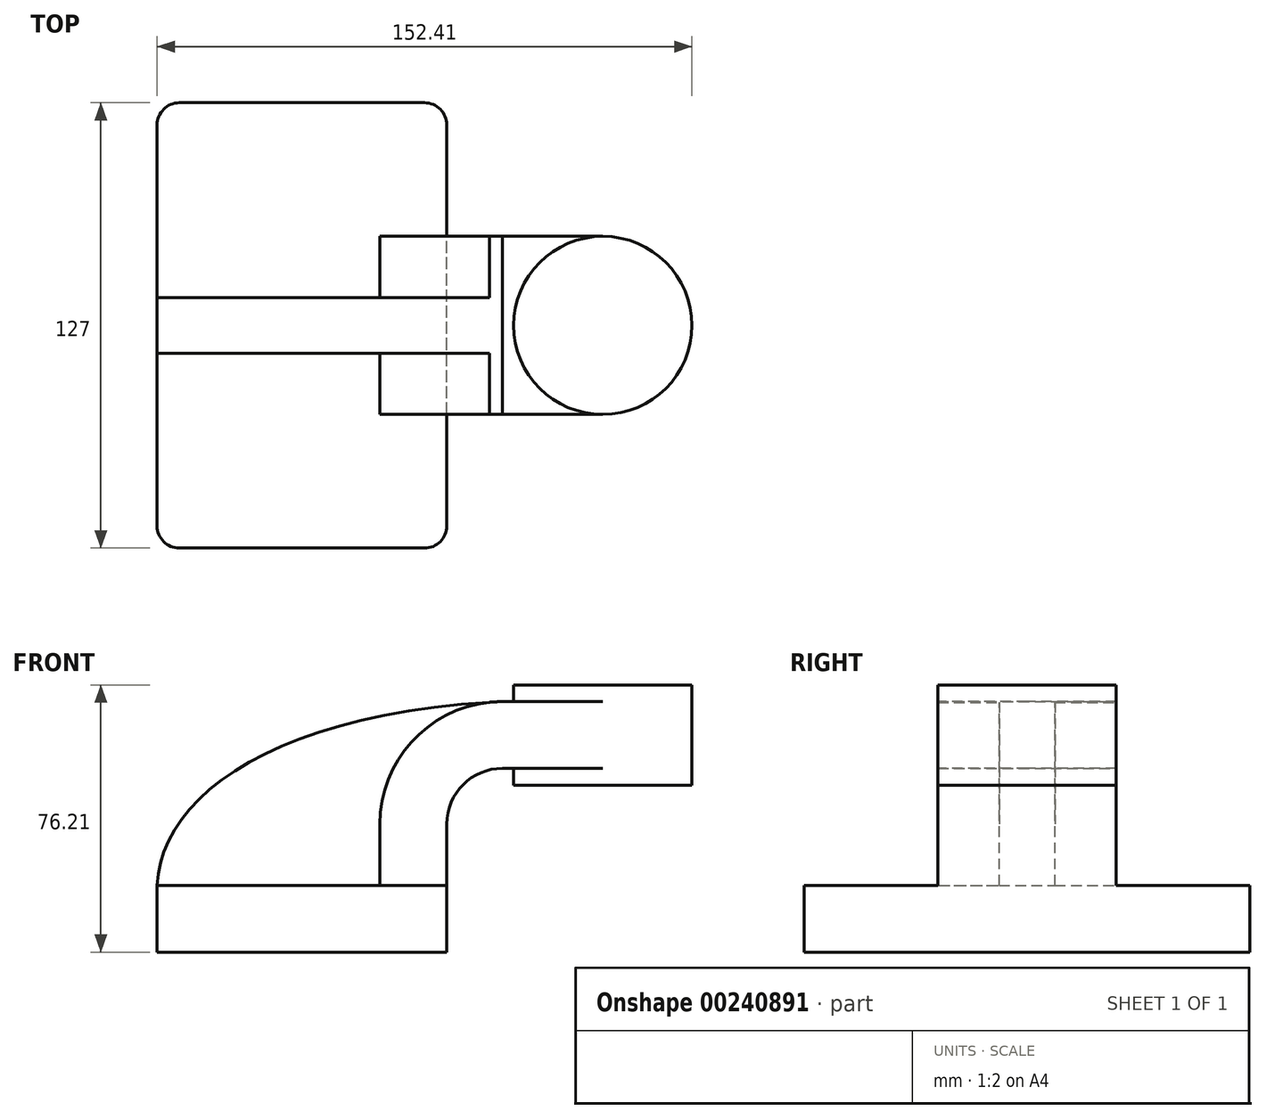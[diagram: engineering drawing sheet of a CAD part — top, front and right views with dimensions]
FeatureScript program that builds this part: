
annotation { "Feature Type Name" : "Feature", "Feature Type Description" : "" }
export const myFeature = defineFeature(function(context is Context, id is Id, definition is map)
    precondition{}
    {
        {
            var Q0;
            Q0=qCreatedBy(makeId("Front.planeOp"),FACE);
            var sketch = newSketch(context, id + "F0", { "sketchPlane" : qUnion([Q0])});
            skLineSegment(sketch, "E0.bottom", {"start": v(41.27, 9.53) * mm, "end": v(-41.28, 9.53) * mm});
            skLineSegment(sketch, "E0.top", {"start": v(41.28, -9.52) * mm, "end": v(-41.27, -9.52) * mm});
            skLineSegment(sketch, "E0.left", {"start": v(41.28, 9.53) * mm, "end": v(41.28, -9.52) * mm});
            skLineSegment(sketch, "E0.right", {"start": v(-41.28, 9.53) * mm, "end": v(-41.27, -9.52) * mm});
            skPoint(sketch, "E0.middle", {"position": v(0, 0) * mm});
            skLineSegment(sketch, "E1.bottom", {"start": v(111.12, 38.1) * mm, "end": v(60.32, 38.1) * mm});
            skLineSegment(sketch, "E1.top", {"start": v(111.12, 66.68) * mm, "end": v(60.32, 66.68) * mm});
            skLineSegment(sketch, "E1.left", {"start": v(111.12, 38.1) * mm, "end": v(111.12, 66.68) * mm});
            skLineSegment(sketch, "E1.right", {"start": v(60.32, 38.1) * mm, "end": v(60.32, 66.68) * mm});
            skPoint(sketch, "E1.middle", {"position": v(85.72, 52.39) * mm});
            skLineSegment(sketch, "E2", {"start": v(41.27, 9.53) * mm, "end": v(41.27, 27) * mm});
            skArc(sketch, "E3", {"start": v(41.27, 27) * mm, "mid": v(45.92, 38.23) * mm, "end": v(57.15, 42.88) * mm});
            skLineSegment(sketch, "E4", {"start": v(57.15, 42.88) * mm, "end": v(98.13, 42.88) * mm});
            skLineSegment(sketch, "E5.0", {"start": v(57.15, 61.93) * mm, "end": v(98.13, 61.93) * mm});
            skArc(sketch, "E5.1", {"start": v(22.23, 27) * mm, "mid": v(32.45, 51.7) * mm, "end": v(57.15, 61.93) * mm});
            skLineSegment(sketch, "E5.2", {"start": v(22.22, 9.53) * mm, "end": v(22.22, 27) * mm});
            skLineSegment(sketch, "E6", {"start": v(85.72, 38.1) * mm, "end": v(85.73, 66.68) * mm});
            skFitSpline(sketch, "E7", {"points": [v(-41.28, 9.52) * mm, v(57.15, 61.93) * mm], "startDerivative": vector(3.13, 75.02) * mm, "endDerivative": vector(196.2, 9.22) * mm});
            skSolve(sketch);
        }
        {
            var Q0;
            Q0=makeQuery(id+"F0.imprint","IMPRINT",FACE,{"disambiguationData":[TD([[makeQuery(id+"F0.imprint","IMPRINT",EDGE,{"derivedFrom":sQuery(id+"F0.wireOp",EDGE,"E0.top")}),-1.0]])]});
            extrude(context, id + "F1", {"entities" : qUnion([Q0]), "endBound" : BoundingType.SYMMETRIC, "depth" : 127 * mm});
        }
        {
            var Q0;
            {var subQ0=sQuery(id+"F0.wireOp",EDGE,"E4");var subQ1=sQuery(id+"F0.wireOp",EDGE,"E1.right");var subQ2=makeQuery(id+"F0.imprint","INTERSECT",VERTEX,{"derivedFrom":[subQ1,subQ0]});Q0=makeQuery(id+"F0.imprint","IMPRINT",FACE,{"disambiguationData":[TD([[makeQuery(id+"F0.imprint","IMPRINT",EDGE,{"disambiguationData":[TD([[subQ2,-1.0]])],"derivedFrom":subQ1}),-1.0]])]});}
            var Q1;
            {var subQ1=sQuery(id+"F0.wireOp",EDGE,"E2");Q1=makeQuery(id+"F0.imprint","IMPRINT",FACE,{"disambiguationData":[TD([[makeQuery(id+"F0.imprint","IMPRINT",EDGE,{"derivedFrom":subQ1}),1.0]])]});}
            extrude(context, id + "F2", {"entities" : qUnion([Q0, Q1]), "operationType" : NewBodyOperationType.ADD, "endBound" : BoundingType.SYMMETRIC, "depth" : 50.8 * mm});
        }
        {
            var Q0;
            {var subQ3=sQuery(id+"F0.wireOp",EDGE,"E5.2");Q0=makeQuery(id+"F0.imprint","IMPRINT",FACE,{"disambiguationData":[TD([[makeQuery(id+"F0.imprint","IMPRINT",EDGE,{"derivedFrom":subQ3}),1.0]])]});}
            extrude(context, id + "F3", {"entities" : qUnion([Q0]), "operationType" : NewBodyOperationType.ADD, "endBound" : BoundingType.SYMMETRIC, "depth" : 15.88 * mm});
        }
        {
            var Q0;
            {var subQ0=sQuery(id+"F0.wireOp",EDGE,"E1.left");Q0=makeQuery(id+"F0.imprint","IMPRINT",FACE,{"disambiguationData":[TD([[makeQuery(id+"F0.imprint","IMPRINT",EDGE,{"derivedFrom":subQ0}),1.0]])]});}
            var Q1;
            Q1=sQuery(id+"F0.wireOp",EDGE,"E6");
            revolve(context, id + "F4", {"operationType" : NewBodyOperationType.ADD, "entities" : qUnion([Q0]), "axis" : qUnion([Q1]), "revolveType" : RevolveType.FULL});
        }
        {
            var Q0;
            Q0=makeQuery(id+"F1.opExtrude","CAP_EDGE",EDGE,{"disambiguationData":[OSD([sQuery(id+"F0.wireOp",EDGE,"E0.left")])],"isStart":false});
            var Q1;
            Q1=makeQuery(id+"F1.opExtrude","CAP_EDGE",EDGE,{"disambiguationData":[OSD([sQuery(id+"F0.wireOp",EDGE,"E0.right")])],"isStart":false});
            var Q2;
            Q2=makeQuery(id+"F1.opExtrude","CAP_EDGE",EDGE,{"disambiguationData":[OSD([sQuery(id+"F0.wireOp",EDGE,"E0.right")])],"isStart":true});
            var Q3;
            Q3=makeQuery(id+"F1.opExtrude","CAP_EDGE",EDGE,{"disambiguationData":[OSD([sQuery(id+"F0.wireOp",EDGE,"E0.left")])],"isStart":true});
            fillet(context, id + "F5", {"entities" : qUnion([Q0, Q1, Q2, Q3]), "radius" : 6.35 * mm, "tangentPropagation" : true, "allowEdgeOverflow" : false});
        }
    });
